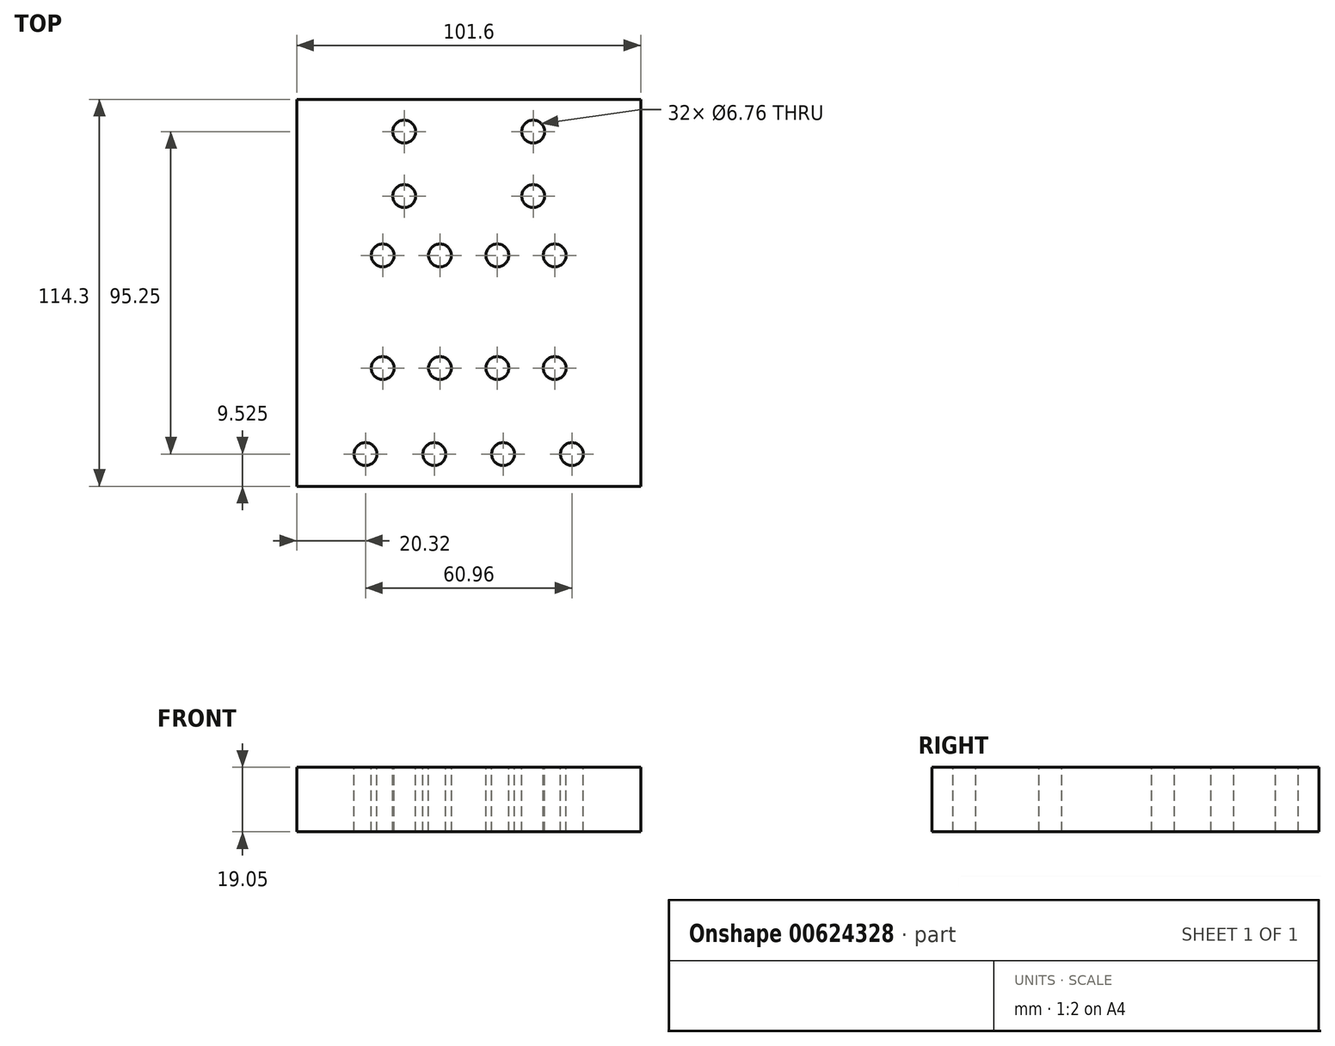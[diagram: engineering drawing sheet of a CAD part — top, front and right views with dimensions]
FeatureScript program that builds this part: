
annotation { "Feature Type Name" : "Feature", "Feature Type Description" : "" }
export const myFeature = defineFeature(function(context is Context, id is Id, definition is map)
    precondition{}
    {
        {
            var Q0;
            Q0=qCreatedBy(makeId("Top.planeOp"),FACE);
            var sketch = newSketch(context, id + "F0", { "sketchPlane" : qUnion([Q0])});
            skLineSegment(sketch, "E0.bottom", {"start": v(-50.8, 57.15) * mm, "end": v(50.8, 57.15) * mm});
            skLineSegment(sketch, "E0.top", {"start": v(-50.8, -57.15) * mm, "end": v(50.8, -57.15) * mm});
            skLineSegment(sketch, "E0.left", {"start": v(-50.8, 57.15) * mm, "end": v(-50.8, -57.15) * mm});
            skLineSegment(sketch, "E0.right", {"start": v(50.8, 57.15) * mm, "end": v(50.8, -57.15) * mm});
            skLineSegment(sketch, "E1", {"start": v(0, 57.15) * mm, "end": v(0, -57.15) * mm, "construction": true});
            skLineSegment(sketch, "E2", {"start": v(-50.8, 0) * mm, "end": v(50.8, 0) * mm, "construction": true});
            skSolve(sketch);
        }
        {
            var Q0;
            Q0=makeQuery(id+"F0.imprint","IMPRINT",FACE,{"disambiguationData":[TD([[makeQuery(id+"F0.imprint","IMPRINT",EDGE,{"derivedFrom":sQuery(id+"F0.wireOp",EDGE,"E0.bottom")}),-1.0]])]});
            extrude(context, id + "F1", {"entities" : qUnion([Q0]), "depth" : 19.05 * mm, "offsetDistance" : 25.4 * mm});
        }
        {
            var Q0;
            Q0=makeQuery(id+"F1.opExtrude","CAP_FACE",FACE,{"disambiguationData":[OSD([sQuery(id+"F0.wireOp",EDGE,"E0.bottom"),sQuery(id+"F0.wireOp",EDGE,"E0.top"),sQuery(id+"F0.wireOp",EDGE,"E0.left"),sQuery(id+"F0.wireOp",EDGE,"E0.right")])],"isStart":false});
            var sketch = newSketch(context, id + "F2", { "sketchPlane" : qUnion([Q0])});
            skLineSegment(sketch, "E3", {"start": v(-50.8, -47.62) * mm, "end": v(50.8, -47.62) * mm, "construction": true});
            skPoint(sketch, "E4", {"position": v(-30.48, -47.63) * mm});
            skPoint(sketch, "E5.1.0.0", {"position": v(-10.16, -47.62) * mm});
            skPoint(sketch, "E5.2.0.0", {"position": v(10.16, -47.62) * mm});
            skPoint(sketch, "E5.3.0.0", {"position": v(30.48, -47.62) * mm});
            skLineSegment(sketch, "E5.direction1", {"start": v(-30.48, -47.62) * mm, "end": v(-10.16, -47.62) * mm, "construction": true});
            skLineSegment(sketch, "E6", {"start": v(-19.05, 57.15) * mm, "end": v(-19.05, -57.15) * mm, "construction": true});
            skPoint(sketch, "E7", {"position": v(-19.05, 47.63) * mm});
            skLineSegment(sketch, "E8.direction1", {"start": v(-19.05, 47.63) * mm, "end": v(19.05, 47.63) * mm, "construction": true});
            skLineSegment(sketch, "E8.direction2", {"start": v(-19.05, 53.98) * mm, "end": v(-19.05, 47.63) * mm, "construction": true});
            skLineSegment(sketch, "E9", {"start": v(-50.8, -22.22) * mm, "end": v(50.8, -22.22) * mm, "construction": true});
            skPoint(sketch, "E10", {"position": v(-25.4, -22.22) * mm});
            skPoint(sketch, "E11.0.1.0", {"position": v(-25.4, 11.07) * mm});
            skPoint(sketch, "E11.1.0.0", {"position": v(-8.47, -22.22) * mm});
            skPoint(sketch, "E11.1.1.0", {"position": v(-8.47, 11.07) * mm});
            skPoint(sketch, "E11.2.0.0", {"position": v(8.47, -22.23) * mm});
            skPoint(sketch, "E11.2.1.0", {"position": v(8.47, 11.07) * mm});
            skPoint(sketch, "E11.3.0.0", {"position": v(25.4, -22.23) * mm});
            skPoint(sketch, "E11.3.1.0", {"position": v(25.4, 11.07) * mm});
            skLineSegment(sketch, "E11.direction1", {"start": v(-25.4, -22.22) * mm, "end": v(-8.47, -22.22) * mm, "construction": true});
            skLineSegment(sketch, "E11.direction2", {"start": v(-25.4, -22.22) * mm, "end": v(-25.4, 11.07) * mm, "construction": true});
            skPoint(sketch, "E12.0.1.0", {"position": v(19.05, 47.63) * mm});
            skPoint(sketch, "E13.0.0.1", {"position": v(-19.05, 28.58) * mm});
            skPoint(sketch, "E13.0.1.1", {"position": v(19.05, 28.58) * mm});
            skSolve(sketch);
        }
        {
            var Q0;
            Q0=sQuery(id+"F2.wireOp",VERTEX,"E4");
            var Q1;
            Q1=sQuery(id+"F2.wireOp",VERTEX,"E5.1.0.0");
            var Q2;
            Q2=sQuery(id+"F2.wireOp",VERTEX,"E5.2.0.0");
            var Q3;
            Q3=sQuery(id+"F2.wireOp",VERTEX,"E5.3.0.0");
            var Q4;
            Q4=sQuery(id+"F2.wireOp",VERTEX,"E8.0.1.0");
            var Q5;
            Q5=sQuery(id+"F2.wireOp",VERTEX,"E7");
            var Q6;
            Q6=sQuery(id+"F2.wireOp",VERTEX,"2fff333e-7df6-447c-8c68-f3aa3d0259c4");
            var Q7;
            Q7=sQuery(id+"F2.wireOp",VERTEX,"78f35a73-b5b8-459a-8434-3fb3f5b3d358.0.1.0");
            var Q8;
            Q8=sQuery(id+"F2.wireOp",VERTEX,"E11.0.1.0");
            var Q9;
            Q9=sQuery(id+"F2.wireOp",VERTEX,"E10");
            var Q10;
            Q10=sQuery(id+"F2.wireOp",VERTEX,"E11.1.0.0");
            var Q11;
            Q11=sQuery(id+"F2.wireOp",VERTEX,"E11.1.1.0");
            var Q12;
            Q12=sQuery(id+"F2.wireOp",VERTEX,"E11.2.1.0");
            var Q13;
            Q13=sQuery(id+"F2.wireOp",VERTEX,"E11.2.0.0");
            var Q14;
            Q14=sQuery(id+"F2.wireOp",VERTEX,"E11.3.0.0");
            var Q15;
            Q15=sQuery(id+"F2.wireOp",VERTEX,"E11.3.1.0");
            var Q16;
            Q16=sQuery(id+"F2.wireOp",VERTEX,"E12.0.1.0");
            var Q17;
            Q17=sQuery(id+"F2.wireOp",VERTEX,"E12.0.2.0");
            var Q18;
            Q18=sQuery(id+"F2.wireOp",VERTEX,"E12.0.3.0");
            var Q19;
            Q19=sQuery(id+"F2.wireOp",VERTEX,"E13.0.0.1");
            var Q20;
            Q20=sQuery(id+"F2.wireOp",VERTEX,"E13.0.1.1");
            var Q21;
            Q21=makeQuery(id+"F1.opExtrude","SWEPT_BODY",BODY,{"disambiguationData":[OSD([sQuery(id+"F0.wireOp",EDGE,"E0.bottom"),sQuery(id+"F0.wireOp",EDGE,"E0.top"),sQuery(id+"F0.wireOp",EDGE,"E0.left"),sQuery(id+"F0.wireOp",EDGE,"E0.right")])]});
            hole(context, id + "F3", {"style" : HoleStyle.SIMPLE, "endStyle" : HoleEndStyle.THROUGH, "standardTappedOrClearance" : lookupTablePath({ "standard" : "ANSI", "fit" : "Normal (ASME)", "size" : "1/4", "type" : "Clearance" }), "standardBlindInLast" : lookupTablePath({ "fit" : "Free", "standard" : "ANSI", "size" : "1/4", "type" : "Clearance" }), "holeDiameter" : 6.76 * mm, "majorDiameter" : 6.35 * mm, "isTappedThrough" : true, "tappedDepth" : 12.7 * mm, "tapClearance" : 3, "startFromSketch" : true, "locations" : qUnion([Q0, Q1, Q2, Q3, Q4, Q5, Q6, Q7, Q8, Q9, Q10, Q11, Q12, Q13, Q14, Q15, Q16, Q17, Q18, Q19, Q20]), "scope" : qUnion([Q21])});
        }
        {
            var Q0;
            Q0=makeQuery(id+"F1.opExtrude","CAP_FACE",FACE,{"disambiguationData":[OSD([sQuery(id+"F0.wireOp",EDGE,"E0.bottom"),sQuery(id+"F0.wireOp",EDGE,"E0.top"),sQuery(id+"F0.wireOp",EDGE,"E0.left"),sQuery(id+"F0.wireOp",EDGE,"E0.right")])],"isStart":false});
            var sketch = newSketch(context, id + "F4", { "sketchPlane" : qUnion([Q0])});
            skLineSegment(sketch, "E14", {"start": v(8.47, -22.22) * mm, "end": v(-8.47, 11.07) * mm, "construction": true});
            skLineSegment(sketch, "E15", {"start": v(8.47, 11.07) * mm, "end": v(-8.47, -22.22) * mm, "construction": true});
            skPoint(sketch, "E16", {"position": v(0, -5.58) * mm});
            skSolve(sketch);
        }
        {
            var Q0;
            Q0=makeQuery(id+"F1.opExtrude","CAP_FACE",FACE,{"disambiguationData":[OSD([sQuery(id+"F0.wireOp",EDGE,"E0.bottom"),sQuery(id+"F0.wireOp",EDGE,"E0.top"),sQuery(id+"F0.wireOp",EDGE,"E0.left"),sQuery(id+"F0.wireOp",EDGE,"E0.right")])],"isStart":true});
            var sketch = newSketch(context, id + "F5", { "sketchPlane" : qUnion([Q0])});
            skLineSegment(sketch, "E17", {"start": v(-8.47, 22.22) * mm, "end": v(8.47, -11.07) * mm, "construction": true});
            skLineSegment(sketch, "E18", {"start": v(-8.47, -11.07) * mm, "end": v(8.47, 22.23) * mm, "construction": true});
            skPoint(sketch, "E19", {"position": v(0, 5.58) * mm});
            skSolve(sketch);
        }
    });
